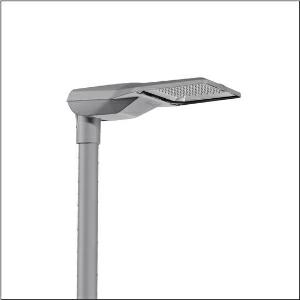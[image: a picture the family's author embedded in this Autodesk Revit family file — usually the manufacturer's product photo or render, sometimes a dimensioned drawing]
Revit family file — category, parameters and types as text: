
# Revit family: streetlight_sl_21_iq_midi___st0_5a_5xe3b31d08nb_970f
name_source: partatom
category: Lighting Fixtures
units: mm (PartAtom-declared; Revit-internal decimal feet)

## family parameters
Cut with Voids When Loaded = No
Host = Face
Light Source = No
Part Type = Normal
Room Calculation Point = No
Round Connector Dimension = Use Diameter
Shared = No

## types (1)
- --- (1 x LED, 23230 lm, 155.5 W, 3000K)
    Apparent Load = 155 VA
    CIE Flux Codes = 43 76 97 100 100
    Color Rendering = 70
    Color Temperature = 3000K
    Default Elevation = 1800 mm
    Description = Streetlight SL 21 iQ midi, mast luminaire, primary light control with lens, of PMMA, primary optical cover: cover, of toughened safety glass, transparent, light distribution: ST0.5a, light emission: direct distribution, primary light characteristic: asymmetric, installation type: post-top, side-entry, LED, High Power LED, rated luminous flux: 23.230lm, luminous efficacy: 149lm/W, light colour: 730, colour temperature: 3000K, control: Auto-Match, Temp-Guard, Lumen-Switch, Night-Set, Smart-Wire, Light-Fading, Desk-Remote (wireless, voltage-free reading and setting of iQ features in the workshop via application-optimized NFC function/RFID function), optimised constant luminous flux control (CLO 2.0), presetting dimming linear, mains connection: 230..240V, AC, 50/60Hz, start of lifetime: 156W, end of service life: 162W, reduction: 69W, luminaire housing, of diecast aluminium, powder-coated, Siteco® metallic grey (DB 702S), corrosivity category C5 mid according to DIN EN ISO 12944, please order mast flange separately, inclination adjustable: 0°, 5°, 10°, 15°, sealing non-destructively replaceable, multi-level sealing system, length: 644mm, width: 335mm, height: 110mm, mast flange for spigot size: 42mm (side-entry): 5XC10008XM4, 60/48mm (side-entry/post-top): 5XC10108XM2, 76/60mm (side-entry/post-top): 5XC10108XM1, protection rating (complete): IP66, insulation class (complete): insulation class II (safety insulation), certification: CE, ENEC, ENEC+, VDE, impact resistance: IK09, permissible operating ambient temperature for outdoor applications: -40..+50°C, standard-compliant lighting for roads and squares, packaging unit: 1 piece

Light Distribution: ST0.5a
    Height = 111 mm
    Lamp = 1 x LED
    Lamp Light Flux = 23230 lm
    Lamp Power = 155.5 W
    Lamp count = 1
    Length = 644 mm
    Luminous efficacy = 149 lm/W
    Manufacturer = Siteco
    ModVariant = No
    Model = 5XE3B31D08NB
    Number of Poles = 1
    OnlyDefault = Yes
    Power Factor = 1
    Product Name = Streetlight SL 21 iQ midi | ST0.5a
    Product group = mast luminaire | pylon top
    ProductGroupID = 6100
    Protection Class = Protection class II
    Protection Degree = IP 66
    RLX_Detail_Level = 1
    RLX_Emergency_Light_Flux = 0 lm
    RLX_Emergency_Type = 0
    RLX_Emergency_Type_DB = No
    RlxData = <blob elided: 102433 chars, md5=1011d506>
    Socket = socket
    Standby Power = 0 W
    System Light Flux = 23230 lm
    System Power = 155 W
    Type Comments = factory setting: luminous flux: 100 % | dim-lin: 254 | 823 mA
    Type Image = l_1004298.jpg
    URL = http://relux.com
    VarID = @adj_104509
    Voltage = 0 V
    Weight = 0.00 kg
    Width = 336 mm

## geometry (parser evidence)
native form markers: Blend x4, Sweep x10
no freeform markers — native parametric forms only
